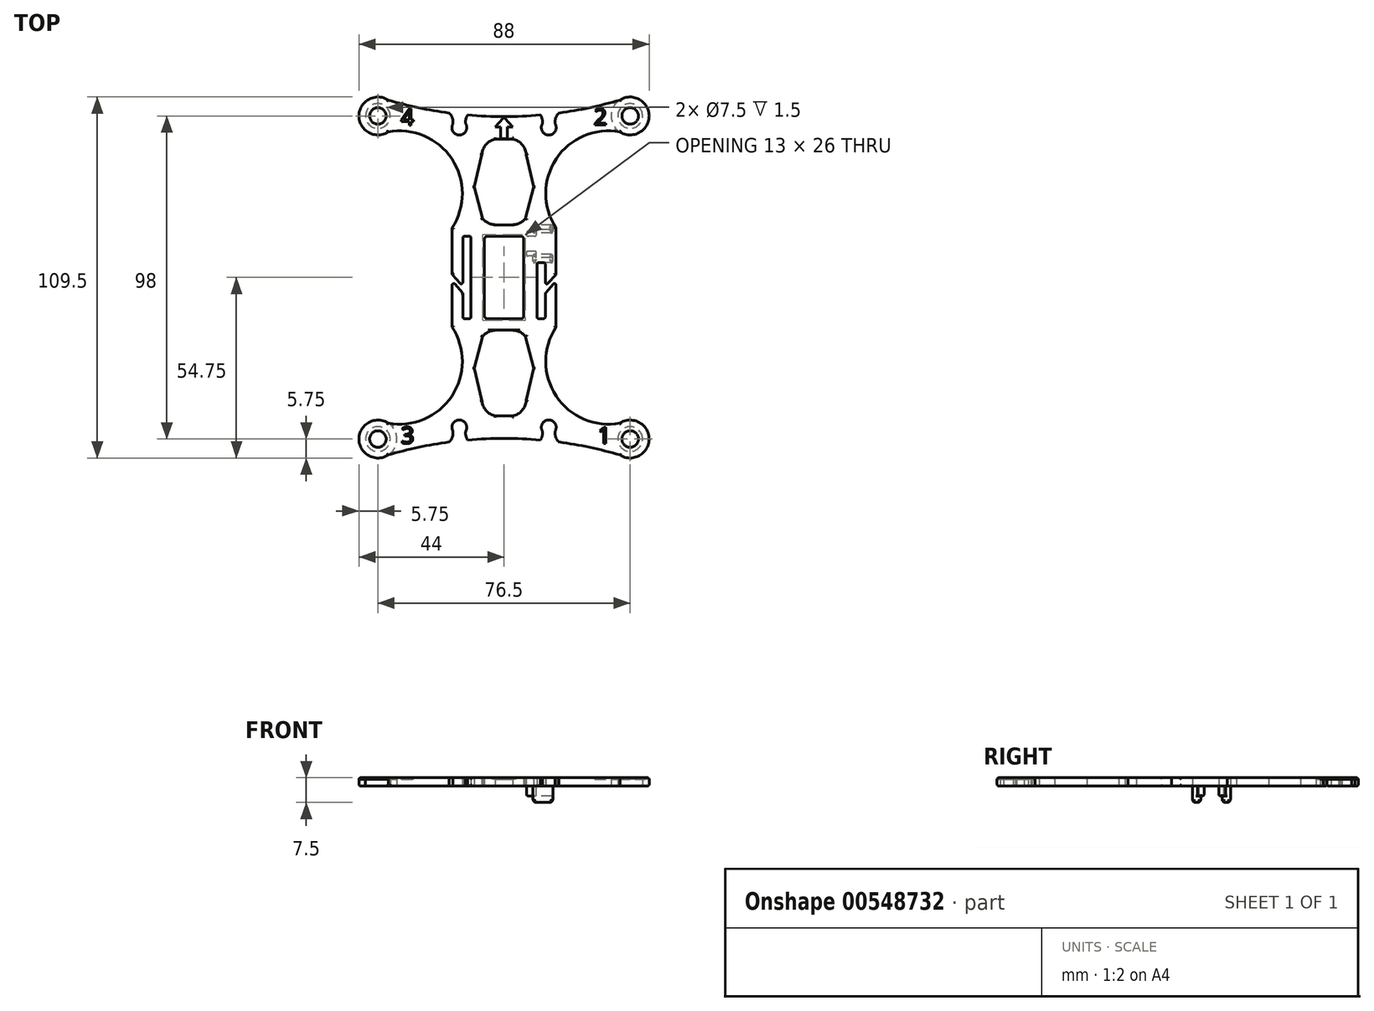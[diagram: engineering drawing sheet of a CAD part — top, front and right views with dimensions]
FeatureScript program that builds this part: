
annotation { "Feature Type Name" : "Feature", "Feature Type Description" : "" }
export const myFeature = defineFeature(function(context is Context, id is Id, definition is map)
    precondition{}
    {
        {
            var Q0;
            Q0=qCreatedBy(makeId("Top.planeOp"),FACE);
            var sketch = newSketch(context, id + "F0", { "sketchPlane" : qUnion([Q0])});
            skPoint(sketch, "E0.middle", {"position": v(0, 0) * mm});
            skCircle(sketch, "E1", {"center": v(-38.25, 49) * mm, "radius": 5.75 * mm});
            skCircle(sketch, "E2.MirrorC", {"center": v(38.25, 49) * mm, "radius": 5.75 * mm});
            skCircle(sketch, "E3.MirrorC", {"center": v(-38.25, -49) * mm, "radius": 5.75 * mm});
            skCircle(sketch, "E4.MirrorC", {"center": v(38.25, -49) * mm, "radius": 5.75 * mm});
            skArc(sketch, "E5", {"start": v(-35.12, 53.82) * mm, "mid": v(-25.97, 51.52) * mm, "end": v(-16.67, 49.9) * mm});
            skCircle(sketch, "E6", {"center": v(-38.25, 49) * mm, "radius": 3.75 * mm});
            skCircle(sketch, "E7.MirrorC", {"center": v(38.25, 49) * mm, "radius": 3.75 * mm});
            skCircle(sketch, "E8.MirrorC", {"center": v(38.25, -49) * mm, "radius": 3.75 * mm});
            skCircle(sketch, "E9.MirrorC", {"center": v(-38.25, -49) * mm, "radius": 3.75 * mm});
            skPoint(sketch, "E10.MirrorP", {"position": v(-9, -27.55) * mm});
            skArc(sketch, "E11.MirrorCS", {"start": v(-2.66, -42) * mm, "mid": v(-5.49, -40.33) * mm, "end": v(-6.7, -37.29) * mm});
            skArc(sketch, "E12.MirrorCS", {"start": v(-2.66, -16) * mm, "mid": v(-4.79, -16.51) * mm, "end": v(-6.5, -17.87) * mm});
            skLineSegment(sketch, "E13", {"start": v(-6.5, -17.87) * mm, "end": v(-9, -27.55) * mm});
            skLineSegment(sketch, "E14", {"start": v(-6.7, -37.29) * mm, "end": v(-9, -27.55) * mm});
            skArc(sketch, "E15.MirrorCS", {"start": v(2.66, -16) * mm, "mid": v(4.79, -16.51) * mm, "end": v(6.5, -17.87) * mm});
            skLineSegment(sketch, "E16.MirrorCS", {"start": v(6.5, -17.87) * mm, "end": v(9, -27.55) * mm});
            skLineSegment(sketch, "E17.MirrorCS", {"start": v(6.7, -37.29) * mm, "end": v(9, -27.55) * mm});
            skArc(sketch, "E18.MirrorCS", {"start": v(2.66, -42) * mm, "mid": v(5.49, -40.33) * mm, "end": v(6.7, -37.29) * mm});
            skLineSegment(sketch, "E19", {"start": v(-2.66, -16) * mm, "end": v(2.66, -16) * mm});
            skLineSegment(sketch, "E20", {"start": v(2.66, -42) * mm, "end": v(-2.66, -42) * mm});
            skLineSegment(sketch, "E21.MirrorCS", {"start": v(-2.66, 16) * mm, "end": v(2.66, 16) * mm});
            skArc(sketch, "E22.MirrorCS", {"start": v(-2.66, 16) * mm, "mid": v(-4.79, 16.51) * mm, "end": v(-6.5, 17.87) * mm});
            skLineSegment(sketch, "E23.MirrorCS", {"start": v(-6.5, 17.87) * mm, "end": v(-9, 27.55) * mm});
            skArc(sketch, "E24.MirrorCS", {"start": v(2.66, 16) * mm, "mid": v(4.79, 16.51) * mm, "end": v(6.5, 17.87) * mm});
            skLineSegment(sketch, "E25.MirrorCS", {"start": v(6.5, 17.87) * mm, "end": v(9, 27.55) * mm});
            skLineSegment(sketch, "E26.MirrorCS", {"start": v(-6.7, 37.29) * mm, "end": v(-9, 27.55) * mm});
            skLineSegment(sketch, "E27.MirrorCS", {"start": v(6.7, 37.29) * mm, "end": v(9, 27.55) * mm});
            skArc(sketch, "E28.MirrorCS", {"start": v(2.66, 42) * mm, "mid": v(5.49, 40.33) * mm, "end": v(6.7, 37.29) * mm});
            skLineSegment(sketch, "E29.MirrorCS", {"start": v(2.66, 42) * mm, "end": v(-2.66, 42) * mm});
            skArc(sketch, "E30.MirrorCS", {"start": v(-2.66, 42) * mm, "mid": v(-5.49, 40.33) * mm, "end": v(-6.7, 37.29) * mm});
            skArc(sketch, "E31", {"start": v(-15.79, 15) * mm, "mid": v(-15.82, 36) * mm, "end": v(-35.17, 44.14) * mm});
            skArc(sketch, "E32.MirrorCS", {"start": v(-35.12, -53.82) * mm, "mid": v(-25.97, -51.52) * mm, "end": v(-16.67, -49.9) * mm});
            skArc(sketch, "E33.MirrorCS", {"start": v(15.79, 15) * mm, "mid": v(15.82, 36) * mm, "end": v(35.17, 44.14) * mm});
            skArc(sketch, "E34.MirrorCS", {"start": v(15.79, -15) * mm, "mid": v(15.82, -36) * mm, "end": v(35.17, -44.14) * mm});
            skArc(sketch, "E35.MirrorCS", {"start": v(-15.79, -15) * mm, "mid": v(-15.82, -36) * mm, "end": v(-35.17, -44.14) * mm});
            skLineSegment(sketch, "E36", {"start": v(-15.79, 15) * mm, "end": v(15.79, 15) * mm, "construction": true});
            skLineSegment(sketch, "E37.MirrorCS", {"start": v(12, -12.5) * mm, "end": v(10.5, -12.5) * mm});
            skArc(sketch, "E38.MirrorCS", {"start": v(12.5, -12) * mm, "mid": v(12.35, -12.35) * mm, "end": v(12, -12.5) * mm});
            skArc(sketch, "E39.MirrorCS", {"start": v(10.5, -12.5) * mm, "mid": v(10.15, -12.35) * mm, "end": v(10, -12) * mm});
            skArc(sketch, "E40.trimOffspring", {"start": v(-11.03, 49.28) * mm, "mid": v(0, 48.79) * mm, "end": v(11.03, 49.28) * mm});
            skArc(sketch, "E41.MirrorCS", {"start": v(-11.6, 46.53) * mm, "mid": v(-11.6, 47.96) * mm, "end": v(-11.03, 49.28) * mm});
            skLineSegment(sketch, "E42.bottom", {"start": v(-5, 12.5) * mm, "end": v(5, 12.5) * mm});
            skLineSegment(sketch, "E42.top", {"start": v(-5, -12.5) * mm, "end": v(5, -12.5) * mm});
            skLineSegment(sketch, "E42.left", {"start": v(-6, 11.5) * mm, "end": v(-6, -11.5) * mm});
            skLineSegment(sketch, "E42.right", {"start": v(6, 11.5) * mm, "end": v(6, -11.5) * mm});
            skPoint(sketch, "E43.visualSharp", {"position": v(-6, 12.5) * mm});
            skArc(sketch, "E43.filletArc", {"start": v(-5, 12.5) * mm, "mid": v(-5.7, 12.2) * mm, "end": v(-6, 11.5) * mm});
            skArc(sketch, "E44.filletArc", {"start": v(6, 11.5) * mm, "mid": v(5.7, 12.2) * mm, "end": v(5, 12.5) * mm});
            skPoint(sketch, "E45.visualSharp", {"position": v(6, -12.5) * mm});
            skArc(sketch, "E45.filletArc", {"start": v(5, -12.5) * mm, "mid": v(5.7, -12.2) * mm, "end": v(6, -11.5) * mm});
            skPoint(sketch, "E46.visualSharp", {"position": v(-6, -12.5) * mm});
            skArc(sketch, "E46.filletArc", {"start": v(-6, -11.5) * mm, "mid": v(-5.7, -12.2) * mm, "end": v(-5, -12.5) * mm});
            skLineSegment(sketch, "E47", {"start": v(-15.79, -15) * mm, "end": v(-15.79, -2.33) * mm});
            skLineSegment(sketch, "E48", {"start": v(-15.79, 15) * mm, "end": v(-15.79, 1) * mm});
            skLineSegment(sketch, "E49.MirrorCS", {"start": v(-10, -12) * mm, "end": v(-10, 12) * mm});
            skLineSegment(sketch, "E50.MirrorCS", {"start": v(-12.5, -12) * mm, "end": v(-12.5, -4.77) * mm});
            skLineSegment(sketch, "E51.MirrorCS", {"start": v(-12, 12.5) * mm, "end": v(-10.5, 12.5) * mm});
            skArc(sketch, "E52.MirrorCS", {"start": v(-10, 12) * mm, "mid": v(-10.15, 12.35) * mm, "end": v(-10.5, 12.5) * mm});
            skArc(sketch, "E53.MirrorCS", {"start": v(-12, 12.5) * mm, "mid": v(-12.35, 12.35) * mm, "end": v(-12.5, 12) * mm});
            skArc(sketch, "E54.MirrorCS", {"start": v(-10.5, -12.5) * mm, "mid": v(-10.15, -12.35) * mm, "end": v(-10, -12) * mm});
            skLineSegment(sketch, "E55.MirrorCS", {"start": v(-12, -12.5) * mm, "end": v(-10.5, -12.5) * mm});
            skArc(sketch, "E56.MirrorCS", {"start": v(-12.5, -12) * mm, "mid": v(-12.35, -12.35) * mm, "end": v(-12, -12.5) * mm});
            skLineSegment(sketch, "E57", {"start": v(-14.91, -2) * mm, "end": v(-12.5, -4.77) * mm});
            skLineSegment(sketch, "E58", {"start": v(-15.79, 1) * mm, "end": v(-13.38, -1.76) * mm});
            skLineSegment(sketch, "E59.trimOffspring", {"start": v(-12.5, -1.43) * mm, "end": v(-12.5, 12) * mm});
            skPoint(sketch, "E60.visualSharp", {"position": v(-15.79, -1) * mm});
            skArc(sketch, "E60.filletArc", {"start": v(-14.91, -2) * mm, "mid": v(-15.47, -1.86) * mm, "end": v(-15.79, -2.33) * mm});
            skArc(sketch, "E61.filletArc", {"start": v(-13.38, -1.76) * mm, "mid": v(-12.82, -1.9) * mm, "end": v(-12.5, -1.43) * mm});
            skLineSegment(sketch, "E62.MirrorCS", {"start": v(12.5, -12) * mm, "end": v(12.5, -4.77) * mm});
            skLineSegment(sketch, "E63.MirrorCS", {"start": v(10, -12) * mm, "end": v(10, 4) * mm});
            skLineSegment(sketch, "E64.MirrorCS", {"start": v(14.91, -2) * mm, "end": v(12.5, -4.77) * mm});
            skLineSegment(sketch, "E65.MirrorCS", {"start": v(15.79, -15) * mm, "end": v(15.79, -2.33) * mm});
            skArc(sketch, "E66.MirrorCS", {"start": v(14.91, -2) * mm, "mid": v(15.47, -1.86) * mm, "end": v(15.79, -2.33) * mm});
            skArc(sketch, "E67.MirrorCS", {"start": v(13.38, -1.76) * mm, "mid": v(12.82, -1.9) * mm, "end": v(12.5, -1.43) * mm});
            skLineSegment(sketch, "E68.MirrorCS", {"start": v(12.5, -1.43) * mm, "end": v(12.5, 4) * mm});
            skLineSegment(sketch, "E69.MirrorCS", {"start": v(15.79, 1) * mm, "end": v(13.38, -1.76) * mm});
            skLineSegment(sketch, "E70.MirrorCS", {"start": v(15.79, 15) * mm, "end": v(15.79, 1) * mm});
            skPoint(sketch, "E71", {"position": v(10, 4.5) * mm});
            skPoint(sketch, "E72", {"position": v(12.5, 4.5) * mm});
            skLineSegment(sketch, "E73", {"start": v(10.5, 4.5) * mm, "end": v(12, 4.5) * mm});
            skArc(sketch, "E74.filletArc", {"start": v(10.5, 4.5) * mm, "mid": v(10.15, 4.35) * mm, "end": v(10, 4) * mm});
            skArc(sketch, "E75.filletArc", {"start": v(12.5, 4) * mm, "mid": v(12.35, 4.35) * mm, "end": v(12, 4.5) * mm});
            skPoint(sketch, "E76.visualSharp", {"position": v(8.79, 4.5) * mm});
            skPoint(sketch, "E77.visualSharp", {"position": v(14.79, 4.5) * mm});
            skArc(sketch, "E78.trimOffspring", {"start": v(16.67, 49.9) * mm, "mid": v(25.97, 51.52) * mm, "end": v(35.12, 53.82) * mm});
            skArc(sketch, "E79.trimOffspring", {"start": v(16.67, -49.9) * mm, "mid": v(25.97, -51.52) * mm, "end": v(35.12, -53.82) * mm});
            skArc(sketch, "E80.trimOffspring", {"start": v(-11.03, -49.28) * mm, "mid": v(0, -48.79) * mm, "end": v(11.03, -49.28) * mm});
            skLineSegment(sketch, "E81", {"start": v(17.22, 49.98) * mm, "end": v(17.22, 49.98) * mm});
            skLineSegment(sketch, "E82.MirrorCS", {"start": v(17.22, -49.98) * mm, "end": v(17.22, -49.98) * mm});
            skArc(sketch, "E83.MirrorCS", {"start": v(-15.54, 46.53) * mm, "mid": v(-15.65, 48.37) * mm, "end": v(-16.67, 49.9) * mm});
            skArc(sketch, "E84.trimOffspring", {"start": v(-15.54, 46.53) * mm, "mid": v(-13.57, 43.2) * mm, "end": v(-11.6, 46.53) * mm});
            skArc(sketch, "E85.MirrorCS", {"start": v(11.6, 46.53) * mm, "mid": v(11.6, 47.96) * mm, "end": v(11.03, 49.28) * mm});
            skArc(sketch, "E86.MirrorCS", {"start": v(15.54, 46.53) * mm, "mid": v(13.57, 43.2) * mm, "end": v(11.6, 46.53) * mm});
            skArc(sketch, "E87.MirrorCS", {"start": v(15.54, 46.53) * mm, "mid": v(15.65, 48.37) * mm, "end": v(16.67, 49.9) * mm});
            skArc(sketch, "E88.MirrorCS", {"start": v(15.54, -46.53) * mm, "mid": v(13.57, -43.2) * mm, "end": v(11.6, -46.53) * mm});
            skArc(sketch, "E89.MirrorCS", {"start": v(15.54, -46.53) * mm, "mid": v(15.65, -48.37) * mm, "end": v(16.67, -49.9) * mm});
            skArc(sketch, "E90.MirrorCS", {"start": v(11.6, -46.53) * mm, "mid": v(11.6, -47.96) * mm, "end": v(11.03, -49.28) * mm});
            skArc(sketch, "E91.MirrorCS", {"start": v(-15.54, -46.53) * mm, "mid": v(-15.65, -48.37) * mm, "end": v(-16.67, -49.9) * mm});
            skArc(sketch, "E92.MirrorCS", {"start": v(-11.6, -46.53) * mm, "mid": v(-11.6, -47.96) * mm, "end": v(-11.03, -49.28) * mm});
            skArc(sketch, "E93.MirrorCS", {"start": v(-15.54, -46.53) * mm, "mid": v(-13.57, -43.2) * mm, "end": v(-11.6, -46.53) * mm});
            skSolve(sketch);
        }
        {
            var Q0;
            {var subQ4=sQuery(id+"F0.wireOp",EDGE,"E5");Q0=makeQuery(id+"F0.imprint","IMPRINT",FACE,{"disambiguationData":[TD([[makeQuery(id+"F0.imprint","IMPRINT",EDGE,{"derivedFrom":subQ4}),-1.0]])]});}
            var Q1;
            {var subQ0=sQuery(id+"F0.wireOp",EDGE,"7a08c846-7200-404a-ab22-a396ae0e95b40.MirrorCS");Q1=makeQuery(id+"F0.imprint","IMPRINT",FACE,{"disambiguationData":[TD([[makeQuery(id+"F0.imprint","IMPRINT",EDGE,{"derivedFrom":subQ0}),-1.0]])]});}
            var Q2;
            {var subQ0=sQuery(id+"F0.wireOp",EDGE,"SV39OC4L-nHPT-JrW3-9Lr1-tMvvluVvlcrm");Q2=makeQuery(id+"F0.imprint","IMPRINT",FACE,{"disambiguationData":[TD([[makeQuery(id+"F0.imprint","IMPRINT",EDGE,{"derivedFrom":subQ0}),1.0]])]});}
            var Q3;
            {var subQ2=sQuery(id+"F0.wireOp",EDGE,"KmvPTI4Y-Ru9T-GGZq-2kg1-KeB8K268cKMw.top");Q3=makeQuery(id+"F0.imprint","IMPRINT",FACE,{"disambiguationData":[TD([[makeQuery(id+"F0.imprint","IMPRINT",EDGE,{"derivedFrom":subQ2}),-1.0]])]});}
            var Q4;
            Q4=makeQuery(id+"F0.imprint","IMPRINT",FACE,{"disambiguationData":[TD([[makeQuery(id+"F0.imprint","IMPRINT",EDGE,{"derivedFrom":sQuery(id+"F0.wireOp",EDGE,"TM0b15PC-G09Y-eCJG-wMI8-OMJ6jJeQZKML.top")}),1.0]])]});
            var Q5;
            Q5=makeQuery(id+"F0.imprint","IMPRINT",FACE,{"disambiguationData":[TD([[makeQuery(id+"F0.imprint","IMPRINT",EDGE,{"derivedFrom":sQuery(id+"F0.wireOp",EDGE,"3d6d2522-cb81-429b-89e0-43078ca379200.MirrorCS")}),-1.0]])]});
            var Q6;
            {var subQ1=sQuery(id+"F0.wireOp",EDGE,"f26be708-061c-449e-934f-b77e1b1d895a0.MirrorCS");Q6=makeQuery(id+"F0.imprint","IMPRINT",FACE,{"disambiguationData":[TD([[makeQuery(id+"F0.imprint","IMPRINT",EDGE,{"derivedFrom":subQ1}),-1.0]])]});}
            extrude(context, id + "F1", {"entities" : qUnion([Q0, Q1, Q2, Q3, Q4, Q5, Q6]), "depth" : 2.5 * mm});
        }
        {
            var Q0;
            Q0=makeQuery(id+"F0.imprint","IMPRINT",FACE,{"disambiguationData":[TD([[makeQuery(id+"F0.imprint","IMPRINT",EDGE,{"derivedFrom":sQuery(id+"F0.wireOp",EDGE,"E6")}),-1.0]])]});
            var Q1;
            Q1=makeQuery(id+"F0.imprint","IMPRINT",FACE,{"disambiguationData":[TD([[makeQuery(id+"F0.imprint","IMPRINT",EDGE,{"derivedFrom":sQuery(id+"F0.wireOp",EDGE,"E7.MirrorC")}),1.0]])]});
            var Q2;
            Q2=makeQuery(id+"F0.imprint","IMPRINT",FACE,{"disambiguationData":[TD([[makeQuery(id+"F0.imprint","IMPRINT",EDGE,{"derivedFrom":sQuery(id+"F0.wireOp",EDGE,"E8.MirrorC")}),-1.0]])]});
            var Q3;
            Q3=makeQuery(id+"F0.imprint","IMPRINT",FACE,{"disambiguationData":[TD([[makeQuery(id+"F0.imprint","IMPRINT",EDGE,{"derivedFrom":sQuery(id+"F0.wireOp",EDGE,"E9.MirrorC")}),1.0]])]});
            extrude(context, id + "F2", {"entities" : qUnion([Q0, Q1, Q2, Q3]), "operationType" : NewBodyOperationType.ADD, "depth" : 2 * mm});
        }
        {
            var Q0;
            Q0=makeQuery(id+"F1.opExtrude","CAP_FACE",FACE,{"disambiguationData":[OSD([sQuery(id+"F0.wireOp",EDGE,"E1"),sQuery(id+"F0.wireOp",EDGE,"E2.MirrorC"),sQuery(id+"F0.wireOp",EDGE,"E3.MirrorC"),sQuery(id+"F0.wireOp",EDGE,"E4.MirrorC"),sQuery(id+"F0.wireOp",EDGE,"E5"),sQuery(id+"F0.wireOp",EDGE,"E6"),sQuery(id+"F0.wireOp",EDGE,"E7.MirrorC"),sQuery(id+"F0.wireOp",EDGE,"E8.MirrorC"),sQuery(id+"F0.wireOp",EDGE,"E9.MirrorC"),sQuery(id+"F0.wireOp",EDGE,"vB4YpJxw-nM1r-KAMU-Z2z7-AA1Xbjjr12VQ"),sQuery(id+"F0.wireOp",EDGE,"e54bd452-817c-44b1-b4a1-4a82a5b737490.MirrorC"),sQuery(id+"F0.wireOp",EDGE,"5ae8c34d-aa19-45d0-b816-4b0481c35e6e0.MirrorC"),sQuery(id+"F0.wireOp",EDGE,"3a3e3443-e76c-4b3f-931a-bba0a9ca54bb0.MirrorC"),sQuery(id+"F0.wireOp",EDGE,"E11.MirrorCS"),sQuery(id+"F0.wireOp",EDGE,"E12.MirrorCS"),sQuery(id+"F0.wireOp",EDGE,"E13"),sQuery(id+"F0.wireOp",EDGE,"E14"),sQuery(id+"F0.wireOp",EDGE,"E15.MirrorCS"),sQuery(id+"F0.wireOp",EDGE,"E16.MirrorCS"),sQuery(id+"F0.wireOp",EDGE,"E17.MirrorCS"),sQuery(id+"F0.wireOp",EDGE,"E18.MirrorCS"),sQuery(id+"F0.wireOp",EDGE,"E19"),sQuery(id+"F0.wireOp",EDGE,"E20"),sQuery(id+"F0.wireOp",EDGE,"E21.MirrorCS"),sQuery(id+"F0.wireOp",EDGE,"E22.MirrorCS"),sQuery(id+"F0.wireOp",EDGE,"E23.MirrorCS"),sQuery(id+"F0.wireOp",EDGE,"E24.MirrorCS"),sQuery(id+"F0.wireOp",EDGE,"E25.MirrorCS"),sQuery(id+"F0.wireOp",EDGE,"E26.MirrorCS"),sQuery(id+"F0.wireOp",EDGE,"E27.MirrorCS"),sQuery(id+"F0.wireOp",EDGE,"E28.MirrorCS"),sQuery(id+"F0.wireOp",EDGE,"E29.MirrorCS"),sQuery(id+"F0.wireOp",EDGE,"E30.MirrorCS"),sQuery(id+"F0.wireOp",EDGE,"E31"),sQuery(id+"F0.wireOp",EDGE,"E32.MirrorCS"),sQuery(id+"F0.wireOp",EDGE,"E33.MirrorCS"),sQuery(id+"F0.wireOp",EDGE,"E34.MirrorCS"),sQuery(id+"F0.wireOp",EDGE,"E35.MirrorCS"),sQuery(id+"F0.wireOp",EDGE,"fVDweLas-wsoK-wS6S-1z9Y-dXXYinH5IBTg"),sQuery(id+"F0.wireOp",EDGE,"DgQ3zJUJ-pF02-0TgB-KWvi-qXfrHXNG7Bep.bottom"),sQuery(id+"F0.wireOp",EDGE,"DgQ3zJUJ-pF02-0TgB-KWvi-qXfrHXNG7Bep.top"),sQuery(id+"F0.wireOp",EDGE,"DgQ3zJUJ-pF02-0TgB-KWvi-qXfrHXNG7Bep.left"),sQuery(id+"F0.wireOp",EDGE,"DgQ3zJUJ-pF02-0TgB-KWvi-qXfrHXNG7Bep.right"),sQuery(id+"F0.wireOp",EDGE,"c76fb391-d7de-4dc3-a68f-2a06cb2f6573.filletArc"),sQuery(id+"F0.wireOp",EDGE,"5654feee-e0ec-4d14-bcde-d39bc1d4a277.filletArc"),sQuery(id+"F0.wireOp",EDGE,"a181469e-c1a0-4d89-87a1-cba4924c182a.filletArc"),sQuery(id+"F0.wireOp",EDGE,"6285ec27-b856-43d4-bfe6-c4aa6bb2cc4e.filletArc"),sQuery(id+"F0.wireOp",EDGE,"E37.MirrorCS"),sQuery(id+"F0.wireOp",EDGE,"E38.MirrorCS"),sQuery(id+"F0.wireOp",EDGE,"E39.MirrorCS"),sQuery(id+"F0.wireOp",EDGE,"6c157492-324c-4fe9-82e5-da5673b074dd0.MirrorCS"),sQuery(id+"F0.wireOp",EDGE,"5ab077b0-c7e9-45b7-be53-f71d1ae10c3f0.MirrorCS"),sQuery(id+"F0.wireOp",EDGE,"fc55cce6-b858-4ce9-87a1-b3bd53c235ab0.MirrorCS"),sQuery(id+"F0.wireOp",EDGE,"9f491082-fd4d-4411-bae9-10bea509d7400.MirrorCS"),sQuery(id+"F0.wireOp",EDGE,"1b0662fc-7704-42c9-b5fa-9ce22a18d3f90.MirrorCS"),sQuery(id+"F0.wireOp",EDGE,"QFYX3ccx-0vfA-8Ihh-7p7o-tATHIodxN48p"),sQuery(id+"F0.wireOp",EDGE,"E40.trimOffspring"),sQuery(id+"F0.wireOp",EDGE,"qH3YTvKd-Peeo-Apzx-g0Uu-npIK0QSimt1m"),sQuery(id+"F0.wireOp",EDGE,"HBzP5cjg-J4kx-zMse-p9Wa-D2NjmpWyf6zF"),sQuery(id+"F0.wireOp",EDGE,"b30a117b-d75a-4502-b387-7b125c7515d1.trimOffspring"),sQuery(id+"F0.wireOp",EDGE,"Q6oGcjuH-qqtT-cDzR-LXAg-flI4N5uVv7ns"),sQuery(id+"F0.wireOp",EDGE,"E41.MirrorCS"),sQuery(id+"F0.wireOp",EDGE,"NQUfp69C-25it-PKYB-2tBc-24tSypLDHoPc"),sQuery(id+"F0.wireOp",EDGE,"c989e6c5-f976-4a01-a2df-d995f657efa90.MirrorCS"),sQuery(id+"F0.wireOp",EDGE,"15c0fab1-d19e-4163-b076-96272f6b97990.MirrorCS"),sQuery(id+"F0.wireOp",EDGE,"37e26e7e-321b-4c47-af7c-8b72d8fa4a340.MirrorCS"),sQuery(id+"F0.wireOp",EDGE,"0fc43aed-00d9-4609-b4de-8f51d0ed3c1b0.MirrorCS"),sQuery(id+"F0.wireOp",EDGE,"ec73fb21-01e8-4369-aab7-f5da74862bec0.MirrorCS"),sQuery(id+"F0.wireOp",EDGE,"92f736b5-5a78-439e-ae92-a389169262630.MirrorCS"),sQuery(id+"F0.wireOp",EDGE,"d2bba0ee-929f-40cb-a0b9-0c6ccd42c60c0.MirrorCS"),sQuery(id+"F0.wireOp",EDGE,"95becd90-c284-490f-9980-00c66b97ee920.MirrorCS"),sQuery(id+"F0.wireOp",EDGE,"17a50fb4-b6d3-4921-a8fa-819a7e347bdf0.MirrorCS"),sQuery(id+"F0.wireOp",EDGE,"0a836e34-2154-49af-98e0-05fdf2c9219c0.MirrorCS"),sQuery(id+"F0.wireOp",EDGE,"69461dee-d267-421c-9efa-fca9b703b25c0.MirrorCS"),sQuery(id+"F0.wireOp",EDGE,"E42.bottom"),sQuery(id+"F0.wireOp",EDGE,"E42.top"),sQuery(id+"F0.wireOp",EDGE,"E42.left"),sQuery(id+"F0.wireOp",EDGE,"E42.right"),sQuery(id+"F0.wireOp",EDGE,"E43.filletArc"),sQuery(id+"F0.wireOp",EDGE,"E44.filletArc"),sQuery(id+"F0.wireOp",EDGE,"E45.filletArc"),sQuery(id+"F0.wireOp",EDGE,"E46.filletArc")])],"isStart":false});
            var sketch = newSketch(context, id + "F3", { "sketchPlane" : qUnion([Q0])});
            skLineSegment(sketch, "E94", {"start": v(-1, 42.11) * mm, "end": v(-1, 45.61) * mm});
            skLineSegment(sketch, "E95", {"start": v(-1, 45.61) * mm, "end": v(-2.66, 45.61) * mm});
            skLineSegment(sketch, "E96", {"start": v(-2.66, 45.61) * mm, "end": v(0, 48.6) * mm});
            skLineSegment(sketch, "E97.MirrorCS", {"start": v(2.66, 45.61) * mm, "end": v(0, 48.6) * mm});
            skLineSegment(sketch, "E98.MirrorCS", {"start": v(1, 45.61) * mm, "end": v(2.66, 45.61) * mm});
            skLineSegment(sketch, "E99.MirrorCS", {"start": v(1, 42.11) * mm, "end": v(1, 45.61) * mm});
            skLineSegment(sketch, "E100", {"start": v(-1, 42.11) * mm, "end": v(1, 42.11) * mm});
            skText(sketch, "E101", { "text": "1", "fontName": "OpenSans-Regular.ttf"});
            skText(sketch, "E102", { "text": "3", "fontName": "OpenSans-Regular.ttf"});
            skText(sketch, "E103", { "text": "2", "fontName": "OpenSans-Regular.ttf"});
            skText(sketch, "E104", { "text": "4", "fontName": "OpenSans-Regular.ttf"});
            const initialGuessF3  = {"E101": [0.02838, -0.05039, 1, 0, 0.005], "E102": [-0.03125, -0.05033, 1, 0, 0.005], "E103": [0.0272, 0.04623, 1, 0, 0.005], "E104": [-0.03125, 0.0462, 1, 0, 0.005]};
            skSetInitialGuess(sketch, initialGuessF3);
            skSolve(sketch);
        }
        {
            var Q0;
            Q0=qSketchRegion(id+"F3",true);
            extrude(context, id + "F4", {"entities" : qUnion([Q0]), "operationType" : NewBodyOperationType.REMOVE, "oppositeDirection" : true, "depth" : .5 * mm});
        }
        {
            var Q0;
            Q0=makeQuery(id+"F1.opExtrude","CAP_FACE",FACE,{"disambiguationData":[OSD([sQuery(id+"F0.wireOp",EDGE,"E1"),sQuery(id+"F0.wireOp",EDGE,"E2.MirrorC"),sQuery(id+"F0.wireOp",EDGE,"E3.MirrorC"),sQuery(id+"F0.wireOp",EDGE,"E4.MirrorC"),sQuery(id+"F0.wireOp",EDGE,"E5"),sQuery(id+"F0.wireOp",EDGE,"E6"),sQuery(id+"F0.wireOp",EDGE,"E7.MirrorC"),sQuery(id+"F0.wireOp",EDGE,"E8.MirrorC"),sQuery(id+"F0.wireOp",EDGE,"E9.MirrorC"),sQuery(id+"F0.wireOp",EDGE,"vB4YpJxw-nM1r-KAMU-Z2z7-AA1Xbjjr12VQ"),sQuery(id+"F0.wireOp",EDGE,"e54bd452-817c-44b1-b4a1-4a82a5b737490.MirrorC"),sQuery(id+"F0.wireOp",EDGE,"5ae8c34d-aa19-45d0-b816-4b0481c35e6e0.MirrorC"),sQuery(id+"F0.wireOp",EDGE,"3a3e3443-e76c-4b3f-931a-bba0a9ca54bb0.MirrorC"),sQuery(id+"F0.wireOp",EDGE,"E11.MirrorCS"),sQuery(id+"F0.wireOp",EDGE,"E12.MirrorCS"),sQuery(id+"F0.wireOp",EDGE,"E13"),sQuery(id+"F0.wireOp",EDGE,"E14"),sQuery(id+"F0.wireOp",EDGE,"E15.MirrorCS"),sQuery(id+"F0.wireOp",EDGE,"E16.MirrorCS"),sQuery(id+"F0.wireOp",EDGE,"E17.MirrorCS"),sQuery(id+"F0.wireOp",EDGE,"E18.MirrorCS"),sQuery(id+"F0.wireOp",EDGE,"E19"),sQuery(id+"F0.wireOp",EDGE,"E20"),sQuery(id+"F0.wireOp",EDGE,"E21.MirrorCS"),sQuery(id+"F0.wireOp",EDGE,"E22.MirrorCS"),sQuery(id+"F0.wireOp",EDGE,"E23.MirrorCS"),sQuery(id+"F0.wireOp",EDGE,"E24.MirrorCS"),sQuery(id+"F0.wireOp",EDGE,"E25.MirrorCS"),sQuery(id+"F0.wireOp",EDGE,"E26.MirrorCS"),sQuery(id+"F0.wireOp",EDGE,"E27.MirrorCS"),sQuery(id+"F0.wireOp",EDGE,"E28.MirrorCS"),sQuery(id+"F0.wireOp",EDGE,"E29.MirrorCS"),sQuery(id+"F0.wireOp",EDGE,"E30.MirrorCS"),sQuery(id+"F0.wireOp",EDGE,"E31"),sQuery(id+"F0.wireOp",EDGE,"E32.MirrorCS"),sQuery(id+"F0.wireOp",EDGE,"E33.MirrorCS"),sQuery(id+"F0.wireOp",EDGE,"E34.MirrorCS"),sQuery(id+"F0.wireOp",EDGE,"E35.MirrorCS"),sQuery(id+"F0.wireOp",EDGE,"E37.MirrorCS"),sQuery(id+"F0.wireOp",EDGE,"E38.MirrorCS"),sQuery(id+"F0.wireOp",EDGE,"E39.MirrorCS"),sQuery(id+"F0.wireOp",EDGE,"E40.trimOffspring"),sQuery(id+"F0.wireOp",EDGE,"qH3YTvKd-Peeo-Apzx-g0Uu-npIK0QSimt1m"),sQuery(id+"F0.wireOp",EDGE,"HBzP5cjg-J4kx-zMse-p9Wa-D2NjmpWyf6zF"),sQuery(id+"F0.wireOp",EDGE,"b30a117b-d75a-4502-b387-7b125c7515d1.trimOffspring"),sQuery(id+"F0.wireOp",EDGE,"Q6oGcjuH-qqtT-cDzR-LXAg-flI4N5uVv7ns"),sQuery(id+"F0.wireOp",EDGE,"E41.MirrorCS"),sQuery(id+"F0.wireOp",EDGE,"NQUfp69C-25it-PKYB-2tBc-24tSypLDHoPc"),sQuery(id+"F0.wireOp",EDGE,"c989e6c5-f976-4a01-a2df-d995f657efa90.MirrorCS"),sQuery(id+"F0.wireOp",EDGE,"15c0fab1-d19e-4163-b076-96272f6b97990.MirrorCS"),sQuery(id+"F0.wireOp",EDGE,"37e26e7e-321b-4c47-af7c-8b72d8fa4a340.MirrorCS"),sQuery(id+"F0.wireOp",EDGE,"0fc43aed-00d9-4609-b4de-8f51d0ed3c1b0.MirrorCS"),sQuery(id+"F0.wireOp",EDGE,"ec73fb21-01e8-4369-aab7-f5da74862bec0.MirrorCS"),sQuery(id+"F0.wireOp",EDGE,"92f736b5-5a78-439e-ae92-a389169262630.MirrorCS"),sQuery(id+"F0.wireOp",EDGE,"d2bba0ee-929f-40cb-a0b9-0c6ccd42c60c0.MirrorCS"),sQuery(id+"F0.wireOp",EDGE,"95becd90-c284-490f-9980-00c66b97ee920.MirrorCS"),sQuery(id+"F0.wireOp",EDGE,"17a50fb4-b6d3-4921-a8fa-819a7e347bdf0.MirrorCS"),sQuery(id+"F0.wireOp",EDGE,"0a836e34-2154-49af-98e0-05fdf2c9219c0.MirrorCS"),sQuery(id+"F0.wireOp",EDGE,"69461dee-d267-421c-9efa-fca9b703b25c0.MirrorCS"),sQuery(id+"F0.wireOp",EDGE,"E42.bottom"),sQuery(id+"F0.wireOp",EDGE,"E42.top"),sQuery(id+"F0.wireOp",EDGE,"E42.left"),sQuery(id+"F0.wireOp",EDGE,"E42.right"),sQuery(id+"F0.wireOp",EDGE,"E43.filletArc"),sQuery(id+"F0.wireOp",EDGE,"E44.filletArc"),sQuery(id+"F0.wireOp",EDGE,"E45.filletArc"),sQuery(id+"F0.wireOp",EDGE,"E46.filletArc"),sQuery(id+"F0.wireOp",EDGE,"E47"),sQuery(id+"F0.wireOp",EDGE,"E48"),sQuery(id+"F0.wireOp",EDGE,"E49.MirrorCS"),sQuery(id+"F0.wireOp",EDGE,"E50.MirrorCS"),sQuery(id+"F0.wireOp",EDGE,"E51.MirrorCS"),sQuery(id+"F0.wireOp",EDGE,"E52.MirrorCS"),sQuery(id+"F0.wireOp",EDGE,"E53.MirrorCS"),sQuery(id+"F0.wireOp",EDGE,"E54.MirrorCS"),sQuery(id+"F0.wireOp",EDGE,"E55.MirrorCS"),sQuery(id+"F0.wireOp",EDGE,"E56.MirrorCS"),sQuery(id+"F0.wireOp",EDGE,"E57"),sQuery(id+"F0.wireOp",EDGE,"E58"),sQuery(id+"F0.wireOp",EDGE,"E59.trimOffspring"),sQuery(id+"F0.wireOp",EDGE,"E60.filletArc"),sQuery(id+"F0.wireOp",EDGE,"E61.filletArc"),sQuery(id+"F0.wireOp",EDGE,"E62.MirrorCS"),sQuery(id+"F0.wireOp",EDGE,"E63.MirrorCS"),sQuery(id+"F0.wireOp",EDGE,"E64.MirrorCS"),sQuery(id+"F0.wireOp",EDGE,"E65.MirrorCS"),sQuery(id+"F0.wireOp",EDGE,"E66.MirrorCS"),sQuery(id+"F0.wireOp",EDGE,"E67.MirrorCS"),sQuery(id+"F0.wireOp",EDGE,"E68.MirrorCS"),sQuery(id+"F0.wireOp",EDGE,"E69.MirrorCS"),sQuery(id+"F0.wireOp",EDGE,"E70.MirrorCS"),sQuery(id+"F0.wireOp",EDGE,"E73"),sQuery(id+"F0.wireOp",EDGE,"E74.filletArc"),sQuery(id+"F0.wireOp",EDGE,"E75.filletArc")])],"isStart":true});
            var sketch = newSketch(context, id + "F5", { "sketchPlane" : qUnion([Q0])});
            skLineSegment(sketch, "E105.bottom", {"start": v(14.29, -4.5) * mm, "end": v(9.29, -4.5) * mm});
            skLineSegment(sketch, "E105.top", {"start": v(14.29, -6) * mm, "end": v(9.79, -6) * mm});
            skLineSegment(sketch, "E105.left", {"start": v(14.79, -5) * mm, "end": v(14.79, -5.5) * mm});
            skLineSegment(sketch, "E105.right", {"start": v(8.79, -5) * mm, "end": v(8.79, -6) * mm});
            skLineSegment(sketch, "E106.left", {"start": v(9.79, -6) * mm, "end": v(9.79, -6.5) * mm});
            skLineSegment(sketch, "E106.right", {"start": v(8.79, -6) * mm, "end": v(8.79, -6.5) * mm});
            skLineSegment(sketch, "E107.bottom", {"start": v(8.79, -6.5) * mm, "end": v(7.29, -6.5) * mm});
            skLineSegment(sketch, "E107.top", {"start": v(9.29, -8) * mm, "end": v(7.29, -8) * mm});
            skLineSegment(sketch, "E107.left", {"start": v(9.79, -6.5) * mm, "end": v(9.79, -7.5) * mm});
            skLineSegment(sketch, "E107.right", {"start": v(6.79, -7) * mm, "end": v(6.79, -7.5) * mm});
            skPoint(sketch, "E108.visualSharp", {"position": v(6.79, -6.5) * mm});
            skArc(sketch, "E108.filletArc", {"start": v(7.29, -6.5) * mm, "mid": v(6.94, -6.65) * mm, "end": v(6.79, -7) * mm});
            skPoint(sketch, "E109.visualSharp", {"position": v(6.79, -8) * mm});
            skArc(sketch, "E109.filletArc", {"start": v(6.79, -7.5) * mm, "mid": v(6.94, -7.85) * mm, "end": v(7.29, -8) * mm});
            skPoint(sketch, "E110.visualSharp", {"position": v(9.79, -8) * mm});
            skArc(sketch, "E110.filletArc", {"start": v(9.29, -8) * mm, "mid": v(9.64, -7.85) * mm, "end": v(9.79, -7.5) * mm});
            skPoint(sketch, "E111.visualSharp", {"position": v(14.79, -6) * mm});
            skArc(sketch, "E111.filletArc", {"start": v(14.29, -6) * mm, "mid": v(14.64, -5.85) * mm, "end": v(14.79, -5.5) * mm});
            skPoint(sketch, "E112", {"position": v(14.79, -4.5) * mm});
            skArc(sketch, "E113.filletArc", {"start": v(14.79, -5) * mm, "mid": v(14.64, -4.65) * mm, "end": v(14.29, -4.5) * mm});
            skPoint(sketch, "E114", {"position": v(8.79, -4.5) * mm});
            skArc(sketch, "E115.filletArc", {"start": v(9.29, -4.5) * mm, "mid": v(8.94, -4.65) * mm, "end": v(8.79, -5) * mm});
            skLineSegment(sketch, "E116", {"start": v(6.79, -8) * mm, "end": v(6.79, -12.5) * mm, "construction": true});
            skPoint(sketch, "E117", {"position": v(6.79, -10.25) * mm});
            skLineSegment(sketch, "E118", {"start": v(6.79, -10.25) * mm, "end": v(15.79, -10.25) * mm, "construction": true});
            skLineSegment(sketch, "E119.MirrorCS", {"start": v(9.29, -12.5) * mm, "end": v(7.29, -12.5) * mm});
            skArc(sketch, "E120.MirrorCS", {"start": v(6.79, -13) * mm, "mid": v(6.94, -12.65) * mm, "end": v(7.29, -12.5) * mm});
            skLineSegment(sketch, "E121.MirrorCS", {"start": v(6.79, -13.5) * mm, "end": v(6.79, -13) * mm});
            skArc(sketch, "E122.MirrorCS", {"start": v(7.29, -14) * mm, "mid": v(6.94, -13.85) * mm, "end": v(6.79, -13.5) * mm});
            skLineSegment(sketch, "E123.MirrorCS", {"start": v(8.79, -14) * mm, "end": v(7.29, -14) * mm});
            skLineSegment(sketch, "E124.MirrorCS", {"start": v(9.79, -14) * mm, "end": v(9.79, -13) * mm});
            skArc(sketch, "E125.MirrorCS", {"start": v(9.29, -12.5) * mm, "mid": v(9.64, -12.65) * mm, "end": v(9.79, -13) * mm});
            skLineSegment(sketch, "E126.MirrorCS", {"start": v(8.79, -14.5) * mm, "end": v(8.79, -14) * mm});
            skLineSegment(sketch, "E127.MirrorCS", {"start": v(9.79, -14.5) * mm, "end": v(9.79, -14) * mm});
            skLineSegment(sketch, "E128.MirrorCS", {"start": v(8.79, -15.5) * mm, "end": v(8.79, -14.5) * mm});
            skArc(sketch, "E129.MirrorCS", {"start": v(9.29, -16) * mm, "mid": v(8.94, -15.85) * mm, "end": v(8.79, -15.5) * mm});
            skLineSegment(sketch, "E130.MirrorCS", {"start": v(14.29, -14.5) * mm, "end": v(9.79, -14.5) * mm});
            skLineSegment(sketch, "E131.MirrorCS", {"start": v(14.29, -16) * mm, "end": v(9.29, -16) * mm});
            skArc(sketch, "E132.MirrorCS", {"start": v(14.29, -14.5) * mm, "mid": v(14.64, -14.65) * mm, "end": v(14.79, -15) * mm});
            skLineSegment(sketch, "E133.MirrorCS", {"start": v(14.79, -15.5) * mm, "end": v(14.79, -15) * mm});
            skArc(sketch, "E134.MirrorCS", {"start": v(14.79, -15.5) * mm, "mid": v(14.64, -15.85) * mm, "end": v(14.29, -16) * mm});
            skPoint(sketch, "E135.orphan", {"position": v(8.79, -14.5) * mm});
            skSolve(sketch);
        }
        {
            var Q0;
            Q0=qSketchRegion(id+"F5",true);
            extrude(context, id + "F6", {"entities" : qUnion([Q0]), "operationType" : NewBodyOperationType.ADD, "depth" : 3 * mm});
        }
        {
            var Q0;
            Q0=makeQuery(id+"F6.opExtrude","CAP_FACE",FACE,{"disambiguationData":[OSD([sQuery(id+"F5.wireOp",EDGE,"E105.bottom"),sQuery(id+"F5.wireOp",EDGE,"E105.top"),sQuery(id+"F5.wireOp",EDGE,"E105.left"),sQuery(id+"F5.wireOp",EDGE,"E105.right"),sQuery(id+"F5.wireOp",EDGE,"E106.left"),sQuery(id+"F5.wireOp",EDGE,"E106.right"),sQuery(id+"F5.wireOp",EDGE,"E107.bottom"),sQuery(id+"F5.wireOp",EDGE,"E107.top"),sQuery(id+"F5.wireOp",EDGE,"E107.left"),sQuery(id+"F5.wireOp",EDGE,"E107.right"),sQuery(id+"F5.wireOp",EDGE,"E108.filletArc"),sQuery(id+"F5.wireOp",EDGE,"E109.filletArc"),sQuery(id+"F5.wireOp",EDGE,"E110.filletArc"),sQuery(id+"F5.wireOp",EDGE,"E111.filletArc"),sQuery(id+"F5.wireOp",EDGE,"E113.filletArc"),sQuery(id+"F5.wireOp",EDGE,"E115.filletArc")])],"isStart":false});
            var sketch = newSketch(context, id + "F7", { "sketchPlane" : qUnion([Q0])});
            skPoint(sketch, "E136.firstSnap0", {"position": v(14.64, -4.65) * mm});
            skLineSegment(sketch, "E136.bottom", {"start": v(14.29, -4.5) * mm, "end": v(9.29, -4.5) * mm});
            skLineSegment(sketch, "E136.top", {"start": v(14.29, -7) * mm, "end": v(9.29, -7) * mm});
            skLineSegment(sketch, "E136.left", {"start": v(14.79, -5) * mm, "end": v(14.79, -6.5) * mm});
            skLineSegment(sketch, "E136.right", {"start": v(8.79, -5) * mm, "end": v(8.79, -6.5) * mm});
            skPoint(sketch, "E137.visualSharp", {"position": v(14.79, -4.5) * mm});
            skArc(sketch, "E137.filletArc", {"start": v(14.79, -5) * mm, "mid": v(14.64, -4.65) * mm, "end": v(14.29, -4.5) * mm});
            skPoint(sketch, "E138.visualSharp", {"position": v(8.79, -4.5) * mm});
            skArc(sketch, "E138.filletArc", {"start": v(9.29, -4.5) * mm, "mid": v(8.94, -4.65) * mm, "end": v(8.79, -5) * mm});
            skPoint(sketch, "E139.visualSharp", {"position": v(14.79, -7) * mm});
            skArc(sketch, "E139.filletArc", {"start": v(14.29, -7) * mm, "mid": v(14.64, -6.85) * mm, "end": v(14.79, -6.5) * mm});
            skLineSegment(sketch, "E140", {"start": v(8.79, -7) * mm, "end": v(8.79, -13.5) * mm, "construction": true});
            skPoint(sketch, "E141", {"position": v(8.79, -10.25) * mm});
            skLineSegment(sketch, "E142", {"start": v(8.79, -10.25) * mm, "end": v(15.78, -10.25) * mm, "construction": true});
            skLineSegment(sketch, "E143.MirrorCS", {"start": v(14.29, -13.5) * mm, "end": v(9.29, -13.5) * mm});
            skLineSegment(sketch, "E144.MirrorCS", {"start": v(8.79, -15.5) * mm, "end": v(8.79, -14) * mm});
            skLineSegment(sketch, "E145.MirrorCS", {"start": v(14.29, -16) * mm, "end": v(9.29, -16) * mm});
            skArc(sketch, "E146.MirrorCS", {"start": v(9.29, -16) * mm, "mid": v(8.94, -15.85) * mm, "end": v(8.79, -15.5) * mm});
            skArc(sketch, "E147.MirrorCS", {"start": v(14.79, -15.5) * mm, "mid": v(14.64, -15.85) * mm, "end": v(14.29, -16) * mm});
            skLineSegment(sketch, "E148.MirrorCS", {"start": v(14.79, -15.5) * mm, "end": v(14.79, -14) * mm});
            skArc(sketch, "E149.MirrorCS", {"start": v(14.29, -13.5) * mm, "mid": v(14.64, -13.65) * mm, "end": v(14.79, -14) * mm});
            skPoint(sketch, "E150.visualSharp", {"position": v(8.79, -7) * mm});
            skArc(sketch, "E150.filletArc", {"start": v(8.79, -6.5) * mm, "mid": v(8.94, -6.85) * mm, "end": v(9.29, -7) * mm});
            skPoint(sketch, "E151.visualSharp", {"position": v(8.79, -13.5) * mm});
            skArc(sketch, "E151.filletArc", {"start": v(9.29, -13.5) * mm, "mid": v(8.94, -13.65) * mm, "end": v(8.79, -14) * mm});
            skSolve(sketch);
        }
        {
            var Q0;
            Q0=makeQuery(id+"F7.imprint","IMPRINT",FACE,{"disambiguationData":[TD([[makeQuery(id+"F7.imprint","IMPRINT",EDGE,{"derivedFrom":sQuery(id+"F7.wireOp",EDGE,"E143.MirrorCS")}),1.0]])]});
            var Q1;
            Q1=makeQuery(id+"F7.imprint","IMPRINT",FACE,{"disambiguationData":[TD([[makeQuery(id+"F7.imprint","IMPRINT",EDGE,{"derivedFrom":sQuery(id+"F7.wireOp",EDGE,"E136.bottom")}),1.0]])]});
            var Q2;
            {var subQ0=sQuery(id+"F7.wireOp",EDGE,"E139.filletArc");Q2=makeQuery(id+"F7.imprint","IMPRINT",FACE,{"disambiguationData":[TD([[makeQuery(id+"F7.imprint","IMPRINT",EDGE,{"derivedFrom":subQ0}),1.0]])]});}
            extrude(context, id + "F8", {"entities" : qUnion([Q0, Q1, Q2]), "operationType" : NewBodyOperationType.ADD, "depth" : 2 * mm});
        }
        {
            var Q0;
            Q0=makeQuery(id+"F8.opExtrude","CAP_EDGE",EDGE,{"disambiguationData":[OSD([sQuery(id+"F7.wireOp",EDGE,"E145.MirrorCS")])],"isStart":false});
            var Q1;
            Q1=makeQuery(id+"F8.opExtrude","CAP_EDGE",EDGE,{"disambiguationData":[OSD([sQuery(id+"F7.wireOp",EDGE,"E143.MirrorCS")])],"isStart":false});
            var Q2;
            Q2=makeQuery(id+"F8.opExtrude","CAP_EDGE",EDGE,{"disambiguationData":[OSD([sQuery(id+"F7.wireOp",EDGE,"E151.filletArc")])],"isStart":false});
            var Q3;
            Q3=makeQuery(id+"F8.opExtrude","CAP_EDGE",EDGE,{"disambiguationData":[OSD([sQuery(id+"F7.wireOp",EDGE,"E144.MirrorCS")])],"isStart":false});
            var Q4;
            Q4=makeQuery(id+"F8.opExtrude","CAP_EDGE",EDGE,{"disambiguationData":[OSD([sQuery(id+"F7.wireOp",EDGE,"E146.MirrorCS")])],"isStart":false});
            var Q5;
            Q5=makeQuery(id+"F8.opExtrude","CAP_EDGE",EDGE,{"disambiguationData":[OSD([sQuery(id+"F7.wireOp",EDGE,"E147.MirrorCS")])],"isStart":false});
            var Q6;
            Q6=makeQuery(id+"F8.opExtrude","CAP_EDGE",EDGE,{"disambiguationData":[OSD([sQuery(id+"F7.wireOp",EDGE,"E148.MirrorCS")])],"isStart":false});
            var Q7;
            Q7=makeQuery(id+"F8.opExtrude","CAP_EDGE",EDGE,{"disambiguationData":[OSD([sQuery(id+"F7.wireOp",EDGE,"E149.MirrorCS")])],"isStart":false});
            var Q8;
            Q8=makeQuery(id+"F8.opExtrude","CAP_EDGE",EDGE,{"disambiguationData":[OSD([sQuery(id+"F7.wireOp",EDGE,"E136.top")])],"isStart":false});
            var Q9;
            Q9=makeQuery(id+"F8.opExtrude","CAP_EDGE",EDGE,{"disambiguationData":[OSD([sQuery(id+"F7.wireOp",EDGE,"E139.filletArc")])],"isStart":false});
            var Q10;
            Q10=makeQuery(id+"F8.opExtrude","CAP_EDGE",EDGE,{"disambiguationData":[OSD([sQuery(id+"F7.wireOp",EDGE,"E136.left")])],"isStart":false});
            var Q11;
            Q11=makeQuery(id+"F8.opExtrude","CAP_EDGE",EDGE,{"disambiguationData":[OSD([sQuery(id+"F7.wireOp",EDGE,"E136.bottom")])],"isStart":false});
            var Q12;
            Q12=makeQuery(id+"F8.opExtrude","CAP_EDGE",EDGE,{"disambiguationData":[OSD([sQuery(id+"F7.wireOp",EDGE,"E137.filletArc")])],"isStart":false});
            var Q13;
            Q13=makeQuery(id+"F8.opExtrude","CAP_EDGE",EDGE,{"disambiguationData":[OSD([sQuery(id+"F7.wireOp",EDGE,"E138.filletArc")])],"isStart":false});
            var Q14;
            Q14=makeQuery(id+"F8.opExtrude","CAP_EDGE",EDGE,{"disambiguationData":[OSD([sQuery(id+"F7.wireOp",EDGE,"E136.right")])],"isStart":false});
            var Q15;
            Q15=makeQuery(id+"F8.opExtrude","CAP_EDGE",EDGE,{"disambiguationData":[OSD([sQuery(id+"F7.wireOp",EDGE,"E150.filletArc")])],"isStart":false});
            fillet(context, id + "F9", {"entities" : qUnion([Q0, Q1, Q2, Q3, Q4, Q5, Q6, Q7, Q8, Q9, Q10, Q11, Q12, Q13, Q14, Q15]), "radius" : 1 * mm, "tangentPropagation" : true, "allowEdgeOverflow" : false});
        }
        {
            var Q0;
            Q0=makeQuery(id+"F6.opExtrude","CAP_EDGE",EDGE,{"disambiguationData":[OSD([sQuery(id+"F5.wireOp",EDGE,"E122.MirrorCS")])],"isStart":false});
            var Q1;
            Q1=makeQuery(id+"F6.opExtrude","CAP_EDGE",EDGE,{"disambiguationData":[OSD([sQuery(id+"F5.wireOp",EDGE,"E109.filletArc")])],"isStart":false});
            fillet(context, id + "F10", {"entities" : qUnion([Q0, Q1]), "radius" : .5 * mm, "tangentPropagation" : true, "allowEdgeOverflow" : false});
        }
        {
            var Q0;
            Q0=makeQuery(id+"F1.opExtrude","CAP_EDGE",EDGE,{"disambiguationData":[OSD([sQuery(id+"F0.wireOp",EDGE,"E42.left")])],"isStart":false});
            var Q1;
            Q1=makeQuery(id+"F1.opExtrude","CAP_EDGE",EDGE,{"disambiguationData":[OSD([sQuery(id+"F0.wireOp",EDGE,"E20")])],"isStart":false});
            var Q2;
            Q2=makeQuery(id+"F1.opExtrude","CAP_EDGE",EDGE,{"disambiguationData":[OSD([sQuery(id+"F0.wireOp",EDGE,"E12.MirrorCS")])],"isStart":false});
            var Q3;
            Q3=makeQuery(id+"F1.opExtrude","CAP_EDGE",EDGE,{"disambiguationData":[OSD([sQuery(id+"F0.wireOp",EDGE,"E13")])],"isStart":false});
            var Q4;
            Q4=makeQuery(id+"F1.opExtrude","CAP_EDGE",EDGE,{"disambiguationData":[OSD([sQuery(id+"F0.wireOp",EDGE,"E14")])],"isStart":false});
            var Q5;
            Q5=makeQuery(id+"F1.opExtrude","CAP_EDGE",EDGE,{"disambiguationData":[OSD([sQuery(id+"F0.wireOp",EDGE,"E11.MirrorCS")])],"isStart":false});
            var Q6;
            Q6=makeQuery(id+"F1.opExtrude","CAP_EDGE",EDGE,{"disambiguationData":[OSD([sQuery(id+"F0.wireOp",EDGE,"E15.MirrorCS")])],"isStart":false});
            var Q7;
            Q7=makeQuery(id+"F1.opExtrude","CAP_EDGE",EDGE,{"disambiguationData":[OSD([sQuery(id+"F0.wireOp",EDGE,"E16.MirrorCS")])],"isStart":false});
            var Q8;
            Q8=makeQuery(id+"F1.opExtrude","CAP_EDGE",EDGE,{"disambiguationData":[OSD([sQuery(id+"F0.wireOp",EDGE,"E17.MirrorCS")])],"isStart":false});
            var Q9;
            Q9=makeQuery(id+"F1.opExtrude","CAP_EDGE",EDGE,{"disambiguationData":[OSD([sQuery(id+"F0.wireOp",EDGE,"E18.MirrorCS")])],"isStart":false});
            var Q10;
            Q10=makeQuery(id+"F1.opExtrude","CAP_EDGE",EDGE,{"disambiguationData":[OSD([sQuery(id+"F0.wireOp",EDGE,"E30.MirrorCS")])],"isStart":false});
            var Q11;
            Q11=makeQuery(id+"F1.opExtrude","CAP_EDGE",EDGE,{"disambiguationData":[OSD([sQuery(id+"F0.wireOp",EDGE,"E29.MirrorCS")])],"isStart":false});
            var Q12;
            Q12=makeQuery(id+"F1.opExtrude","CAP_EDGE",EDGE,{"disambiguationData":[OSD([sQuery(id+"F0.wireOp",EDGE,"E28.MirrorCS")])],"isStart":false});
            var Q13;
            Q13=makeQuery(id+"F1.opExtrude","CAP_EDGE",EDGE,{"disambiguationData":[OSD([sQuery(id+"F0.wireOp",EDGE,"E27.MirrorCS")])],"isStart":false});
            var Q14;
            Q14=makeQuery(id+"F1.opExtrude","CAP_EDGE",EDGE,{"disambiguationData":[OSD([sQuery(id+"F0.wireOp",EDGE,"E25.MirrorCS")])],"isStart":false});
            var Q15;
            Q15=makeQuery(id+"F1.opExtrude","CAP_EDGE",EDGE,{"disambiguationData":[OSD([sQuery(id+"F0.wireOp",EDGE,"E21.MirrorCS")])],"isStart":false});
            var Q16;
            Q16=makeQuery(id+"F1.opExtrude","CAP_EDGE",EDGE,{"disambiguationData":[OSD([sQuery(id+"F0.wireOp",EDGE,"E24.MirrorCS")])],"isStart":false});
            var Q17;
            Q17=makeQuery(id+"F1.opExtrude","CAP_EDGE",EDGE,{"disambiguationData":[OSD([sQuery(id+"F0.wireOp",EDGE,"E23.MirrorCS")])],"isStart":false});
            var Q18;
            Q18=makeQuery(id+"F1.opExtrude","CAP_EDGE",EDGE,{"disambiguationData":[OSD([sQuery(id+"F0.wireOp",EDGE,"E22.MirrorCS")])],"isStart":false});
            var Q19;
            Q19=makeQuery(id+"F1.opExtrude","CAP_EDGE",EDGE,{"disambiguationData":[OSD([sQuery(id+"F0.wireOp",EDGE,"E26.MirrorCS")])],"isStart":false});
            var Q20;
            Q20=makeQuery(id+"F1.opExtrude","CAP_EDGE",EDGE,{"disambiguationData":[OSD([sQuery(id+"F0.wireOp",EDGE,"E42.right")])],"isStart":true});
            var Q21;
            Q21=makeQuery(id+"F1.opExtrude","CAP_EDGE",EDGE,{"disambiguationData":[OSD([sQuery(id+"F0.wireOp",EDGE,"E25.MirrorCS")])],"isStart":true});
            var Q22;
            Q22=makeQuery(id+"F1.opExtrude","CAP_EDGE",EDGE,{"disambiguationData":[OSD([sQuery(id+"F0.wireOp",EDGE,"E24.MirrorCS")])],"isStart":true});
            var Q23;
            Q23=makeQuery(id+"F1.opExtrude","CAP_EDGE",EDGE,{"disambiguationData":[OSD([sQuery(id+"F0.wireOp",EDGE,"E21.MirrorCS")])],"isStart":true});
            var Q24;
            Q24=makeQuery(id+"F1.opExtrude","CAP_EDGE",EDGE,{"disambiguationData":[OSD([sQuery(id+"F0.wireOp",EDGE,"E23.MirrorCS")])],"isStart":true});
            var Q25;
            Q25=makeQuery(id+"F1.opExtrude","CAP_EDGE",EDGE,{"disambiguationData":[OSD([sQuery(id+"F0.wireOp",EDGE,"E26.MirrorCS")])],"isStart":true});
            var Q26;
            Q26=makeQuery(id+"F1.opExtrude","CAP_EDGE",EDGE,{"disambiguationData":[OSD([sQuery(id+"F0.wireOp",EDGE,"E30.MirrorCS")])],"isStart":true});
            var Q27;
            Q27=makeQuery(id+"F1.opExtrude","CAP_EDGE",EDGE,{"disambiguationData":[OSD([sQuery(id+"F0.wireOp",EDGE,"E29.MirrorCS")])],"isStart":true});
            var Q28;
            Q28=makeQuery(id+"F1.opExtrude","CAP_EDGE",EDGE,{"disambiguationData":[OSD([sQuery(id+"F0.wireOp",EDGE,"E28.MirrorCS")])],"isStart":true});
            var Q29;
            Q29=makeQuery(id+"F1.opExtrude","CAP_EDGE",EDGE,{"disambiguationData":[OSD([sQuery(id+"F0.wireOp",EDGE,"E27.MirrorCS")])],"isStart":true});
            var Q30;
            Q30=makeQuery(id+"F1.opExtrude","CAP_EDGE",EDGE,{"disambiguationData":[OSD([sQuery(id+"F0.wireOp",EDGE,"E17.MirrorCS")])],"isStart":true});
            var Q31;
            Q31=makeQuery(id+"F1.opExtrude","CAP_EDGE",EDGE,{"disambiguationData":[OSD([sQuery(id+"F0.wireOp",EDGE,"E18.MirrorCS")])],"isStart":true});
            var Q32;
            Q32=makeQuery(id+"F1.opExtrude","CAP_EDGE",EDGE,{"disambiguationData":[OSD([sQuery(id+"F0.wireOp",EDGE,"E20")])],"isStart":true});
            var Q33;
            Q33=makeQuery(id+"F1.opExtrude","CAP_EDGE",EDGE,{"disambiguationData":[OSD([sQuery(id+"F0.wireOp",EDGE,"E11.MirrorCS")])],"isStart":true});
            var Q34;
            Q34=makeQuery(id+"F1.opExtrude","CAP_EDGE",EDGE,{"disambiguationData":[OSD([sQuery(id+"F0.wireOp",EDGE,"E14")])],"isStart":true});
            var Q35;
            Q35=makeQuery(id+"F1.opExtrude","CAP_EDGE",EDGE,{"disambiguationData":[OSD([sQuery(id+"F0.wireOp",EDGE,"E13")])],"isStart":true});
            var Q36;
            Q36=makeQuery(id+"F1.opExtrude","CAP_EDGE",EDGE,{"disambiguationData":[OSD([sQuery(id+"F0.wireOp",EDGE,"E16.MirrorCS")])],"isStart":true});
            var Q37;
            Q37=makeQuery(id+"F1.opExtrude","CAP_EDGE",EDGE,{"disambiguationData":[OSD([sQuery(id+"F0.wireOp",EDGE,"E15.MirrorCS")])],"isStart":true});
            var Q38;
            Q38=makeQuery(id+"F1.opExtrude","CAP_EDGE",EDGE,{"disambiguationData":[OSD([sQuery(id+"F0.wireOp",EDGE,"E19")])],"isStart":true});
            var Q39;
            Q39=makeQuery(id+"F1.opExtrude","CAP_EDGE",EDGE,{"disambiguationData":[OSD([sQuery(id+"F0.wireOp",EDGE,"E12.MirrorCS")])],"isStart":true});
            fillet(context, id + "F11", {"entities" : qUnion([Q0, Q1, Q2, Q3, Q4, Q5, Q6, Q7, Q8, Q9, Q10, Q11, Q12, Q13, Q14, Q15, Q16, Q17, Q18, Q19, Q20, Q21, Q22, Q23, Q24, Q25, Q26, Q27, Q28, Q29, Q30, Q31, Q32, Q33, Q34, Q35, Q36, Q37, Q38, Q39]), "radius" : .5 * mm, "tangentPropagation" : true, "allowEdgeOverflow" : false});
        }
        {
            var Q0;
            Q0=makeQuery(id+"F1.opExtrude","CAP_EDGE",EDGE,{"disambiguationData":[OSD([sQuery(id+"F0.wireOp",EDGE,"E49.MirrorCS")])],"isStart":true});
            var Q1;
            Q1=makeQuery(id+"F1.opExtrude","CAP_EDGE",EDGE,{"disambiguationData":[OSD([sQuery(id+"F0.wireOp",EDGE,"E63.MirrorCS")])],"isStart":true});
            var Q2;
            Q2=makeQuery(id+"F1.opExtrude","CAP_EDGE",EDGE,{"disambiguationData":[OSD([sQuery(id+"F0.wireOp",EDGE,"E49.MirrorCS")])],"isStart":false});
            var Q3;
            Q3=makeQuery(id+"F1.opExtrude","CAP_EDGE",EDGE,{"disambiguationData":[OSD([sQuery(id+"F0.wireOp",EDGE,"E63.MirrorCS")])],"isStart":false});
            fillet(context, id + "F12", {"entities" : qUnion([Q0, Q1, Q2, Q3]), "radius" : .5 * mm, "tangentPropagation" : true, "allowEdgeOverflow" : false});
        }
        {
            var Q0;
            Q0=makeQuery(id+"F1.opExtrude","CAP_EDGE",EDGE,{"disambiguationData":[OSD([sQuery(id+"F0.wireOp",EDGE,"E48")])],"isStart":false});
            var Q1;
            Q1=makeQuery(id+"F1.opExtrude","CAP_EDGE",EDGE,{"disambiguationData":[OSD([sQuery(id+"F0.wireOp",EDGE,"E31")])],"isStart":false});
            var Q2;
            Q2=makeQuery(id+"F1.opExtrude","CAP_EDGE",EDGE,{"disambiguationData":[OSD([sQuery(id+"F0.wireOp",EDGE,"E33.MirrorCS")])],"isStart":false});
            var Q3;
            Q3=makeQuery(id+"F1.opExtrude","CAP_EDGE",EDGE,{"disambiguationData":[OSD([sQuery(id+"F0.wireOp",EDGE,"E70.MirrorCS")])],"isStart":false});
            var Q4;
            Q4=makeQuery(id+"F1.opExtrude","CAP_EDGE",EDGE,{"disambiguationData":[OSD([sQuery(id+"F0.wireOp",EDGE,"E65.MirrorCS")])],"isStart":false});
            var Q5;
            Q5=makeQuery(id+"F1.opExtrude","CAP_EDGE",EDGE,{"disambiguationData":[OSD([sQuery(id+"F0.wireOp",EDGE,"E47")])],"isStart":false});
            var Q6;
            Q6=makeQuery(id+"F1.opExtrude","CAP_EDGE",EDGE,{"disambiguationData":[OSD([sQuery(id+"F0.wireOp",EDGE,"29c33aa2-e30d-4d77-a239-c7a4e06ad0fa.trimOffspring")])],"isStart":false});
            var Q7;
            Q7=makeQuery(id+"F1.opExtrude","CAP_EDGE",EDGE,{"disambiguationData":[OSD([sQuery(id+"F0.wireOp",EDGE,"E79.trimOffspring")])],"isStart":false});
            var Q8;
            Q8=makeQuery(id+"F1.opExtrude","CAP_EDGE",EDGE,{"disambiguationData":[OSD([sQuery(id+"F0.wireOp",EDGE,"E34.MirrorCS")])],"isStart":false});
            var Q9;
            Q9=makeQuery(id+"F1.opExtrude","CAP_EDGE",EDGE,{"disambiguationData":[OSD([sQuery(id+"F0.wireOp",EDGE,"E78.trimOffspring")])],"isStart":false});
            var Q10;
            Q10=makeQuery(id+"F1.opExtrude","CAP_EDGE",EDGE,{"disambiguationData":[OSD([sQuery(id+"F0.wireOp",EDGE,"E40.trimOffspring")])],"isStart":false});
            var Q11;
            Q11=makeQuery(id+"F1.opExtrude","CAP_EDGE",EDGE,{"disambiguationData":[OSD([sQuery(id+"F0.wireOp",EDGE,"E5")])],"isStart":false});
            var Q12;
            Q12=makeQuery(id+"F1.opExtrude","CAP_EDGE",EDGE,{"disambiguationData":[OSD([sQuery(id+"F0.wireOp",EDGE,"E33.MirrorCS")])],"isStart":true});
            var Q13;
            Q13=makeQuery(id+"F1.opExtrude","CAP_EDGE",EDGE,{"disambiguationData":[OSD([sQuery(id+"F0.wireOp",EDGE,"E2.MirrorC")])],"isStart":true});
            var Q14;
            Q14=makeQuery(id+"F1.opExtrude","CAP_EDGE",EDGE,{"disambiguationData":[OSD([sQuery(id+"F0.wireOp",EDGE,"E78.trimOffspring")])],"isStart":true});
            var Q15;
            Q15=makeQuery(id+"F1.opExtrude","CAP_EDGE",EDGE,{"disambiguationData":[OSD([sQuery(id+"F0.wireOp",EDGE,"E40.trimOffspring")])],"isStart":true});
            var Q16;
            Q16=makeQuery(id+"F1.opExtrude","CAP_EDGE",EDGE,{"disambiguationData":[OSD([sQuery(id+"F0.wireOp",EDGE,"E5")])],"isStart":true});
            var Q17;
            Q17=makeQuery(id+"F1.opExtrude","CAP_EDGE",EDGE,{"disambiguationData":[OSD([sQuery(id+"F0.wireOp",EDGE,"E1")])],"isStart":true});
            var Q18;
            Q18=makeQuery(id+"F1.opExtrude","CAP_EDGE",EDGE,{"disambiguationData":[OSD([sQuery(id+"F0.wireOp",EDGE,"E31")])],"isStart":true});
            var Q19;
            Q19=makeQuery(id+"F1.opExtrude","CAP_EDGE",EDGE,{"disambiguationData":[OSD([sQuery(id+"F0.wireOp",EDGE,"E48")])],"isStart":true});
            var Q20;
            Q20=makeQuery(id+"F1.opExtrude","CAP_EDGE",EDGE,{"disambiguationData":[OSD([sQuery(id+"F0.wireOp",EDGE,"E47")])],"isStart":true});
            var Q21;
            Q21=makeQuery(id+"F1.opExtrude","CAP_EDGE",EDGE,{"disambiguationData":[OSD([sQuery(id+"F0.wireOp",EDGE,"E70.MirrorCS")])],"isStart":true});
            var Q22;
            Q22=makeQuery(id+"F1.opExtrude","CAP_EDGE",EDGE,{"disambiguationData":[OSD([sQuery(id+"F0.wireOp",EDGE,"E65.MirrorCS")])],"isStart":true});
            var Q23;
            Q23=makeQuery(id+"F1.opExtrude","CAP_EDGE",EDGE,{"disambiguationData":[OSD([sQuery(id+"F0.wireOp",EDGE,"E34.MirrorCS")])],"isStart":true});
            var Q24;
            Q24=makeQuery(id+"F1.opExtrude","CAP_EDGE",EDGE,{"disambiguationData":[OSD([sQuery(id+"F0.wireOp",EDGE,"E35.MirrorCS")])],"isStart":true});
            var Q25;
            Q25=makeQuery(id+"F1.opExtrude","CAP_EDGE",EDGE,{"disambiguationData":[OSD([sQuery(id+"F0.wireOp",EDGE,"E4.MirrorC")])],"isStart":true});
            var Q26;
            Q26=makeQuery(id+"F1.opExtrude","CAP_EDGE",EDGE,{"disambiguationData":[OSD([sQuery(id+"F0.wireOp",EDGE,"E3.MirrorC")])],"isStart":true});
            var Q27;
            Q27=makeQuery(id+"F1.opExtrude","CAP_EDGE",EDGE,{"disambiguationData":[OSD([sQuery(id+"F0.wireOp",EDGE,"29c33aa2-e30d-4d77-a239-c7a4e06ad0fa.trimOffspring")])],"isStart":true});
            var Q28;
            Q28=makeQuery(id+"F1.opExtrude","CAP_EDGE",EDGE,{"disambiguationData":[OSD([sQuery(id+"F0.wireOp",EDGE,"E32.MirrorCS")])],"isStart":true});
            var Q29;
            Q29=makeQuery(id+"F1.opExtrude","CAP_EDGE",EDGE,{"disambiguationData":[OSD([sQuery(id+"F0.wireOp",EDGE,"E79.trimOffspring")])],"isStart":true});
            var Q30;
            Q30=makeQuery(id+"F1.opExtrude","CAP_EDGE",EDGE,{"disambiguationData":[OSD([sQuery(id+"F0.wireOp",EDGE,"E32.MirrorCS")])],"isStart":false});
            var Q31;
            Q31=makeQuery(id+"F1.opExtrude","CAP_EDGE",EDGE,{"disambiguationData":[OSD([sQuery(id+"F0.wireOp",EDGE,"E35.MirrorCS")])],"isStart":false});
            fillet(context, id + "F13", {"entities" : qUnion([Q0, Q1, Q2, Q3, Q4, Q5, Q6, Q7, Q8, Q9, Q10, Q11, Q12, Q13, Q14, Q15, Q16, Q17, Q18, Q19, Q20, Q21, Q22, Q23, Q24, Q25, Q26, Q27, Q28, Q29, Q30, Q31]), "radius" : .5 * mm, "tangentPropagation" : true, "allowEdgeOverflow" : false});
        }
        {
            var Q0;
            Q0=makeQuery(id+"F2.opExtrude","CAP_FACE",FACE,{"disambiguationData":[OSD([sQuery(id+"F0.wireOp",EDGE,"E3.MirrorC"),sQuery(id+"F0.wireOp",EDGE,"E9.MirrorC")])],"isStart":false});
            var sketch = newSketch(context, id + "F14", { "sketchPlane" : qUnion([Q0])});
            skCircle(sketch, "E152", {"center": v(-38.25, -49) * mm, "radius": 5.75 * mm});
            skCircle(sketch, "E153", {"center": v(-38.25, -49) * mm, "radius": 2.5 * mm});
            skCircle(sketch, "E154.MirrorC", {"center": v(38.25, -49) * mm, "radius": 5.75 * mm});
            skCircle(sketch, "E155.MirrorC", {"center": v(38.25, -49) * mm, "radius": 2.5 * mm});
            skCircle(sketch, "E156.MirrorC", {"center": v(-38.25, 49) * mm, "radius": 5.75 * mm});
            skCircle(sketch, "E157.MirrorC", {"center": v(-38.25, 49) * mm, "radius": 2.5 * mm});
            skCircle(sketch, "E158.MirrorC", {"center": v(38.25, 49) * mm, "radius": 5.75 * mm});
            skCircle(sketch, "E159.MirrorC", {"center": v(38.25, 49) * mm, "radius": 2.5 * mm});
            skSolve(sketch);
        }
        {
            var Q0;
            Q0=qSketchRegion(id+"F14",true);
            extrude(context, id + "F15", {"entities" : qUnion([Q0]), "operationType" : NewBodyOperationType.ADD, "depth" : .5 * mm});
        }
        {
            var Q0;
            Q0=makeQuery(id+"F2.opExtrude","CAP_EDGE",EDGE,{"disambiguationData":[OSD([sQuery(id+"F0.wireOp",EDGE,"E9.MirrorC")])],"isStart":true});
            var Q1;
            Q1=makeQuery(id+"F15.opExtrude","CAP_EDGE",EDGE,{"disambiguationData":[OSD([sQuery(id+"F14.wireOp",EDGE,"E153")])],"isStart":false});
            var Q2;
            Q2=makeQuery(id+"F15.opExtrude","CAP_EDGE",EDGE,{"disambiguationData":[OSD([sQuery(id+"F14.wireOp",EDGE,"E152")])],"isStart":false});
            var Q3;
            Q3=makeQuery(id+"F2.opExtrude","CAP_EDGE",EDGE,{"disambiguationData":[OSD([sQuery(id+"F0.wireOp",EDGE,"E3.MirrorC")])],"isStart":true});
            var Q4;
            Q4=makeQuery(id+"F15.opExtrude","CAP_EDGE",EDGE,{"disambiguationData":[OSD([sQuery(id+"F14.wireOp",EDGE,"E154.MirrorC")])],"isStart":false});
            var Q5;
            Q5=makeQuery(id+"F15.opExtrude","CAP_EDGE",EDGE,{"disambiguationData":[OSD([sQuery(id+"F14.wireOp",EDGE,"E155.MirrorC")])],"isStart":false});
            var Q6;
            Q6=makeQuery(id+"F2.opExtrude","CAP_EDGE",EDGE,{"disambiguationData":[OSD([sQuery(id+"F0.wireOp",EDGE,"E4.MirrorC")])],"isStart":true});
            var Q7;
            Q7=makeQuery(id+"F2.opExtrude","CAP_EDGE",EDGE,{"disambiguationData":[OSD([sQuery(id+"F0.wireOp",EDGE,"E7.MirrorC")])],"isStart":true});
            var Q8;
            Q8=makeQuery(id+"F15.opExtrude","CAP_EDGE",EDGE,{"disambiguationData":[OSD([sQuery(id+"F14.wireOp",EDGE,"E159.MirrorC")])],"isStart":false});
            var Q9;
            Q9=makeQuery(id+"F15.opExtrude","CAP_EDGE",EDGE,{"disambiguationData":[OSD([sQuery(id+"F14.wireOp",EDGE,"E158.MirrorC")])],"isStart":false});
            var Q10;
            Q10=makeQuery(id+"F2.opExtrude","CAP_EDGE",EDGE,{"disambiguationData":[OSD([sQuery(id+"F0.wireOp",EDGE,"E2.MirrorC")])],"isStart":true});
            var Q11;
            Q11=makeQuery(id+"F2.opExtrude","CAP_EDGE",EDGE,{"disambiguationData":[OSD([sQuery(id+"F0.wireOp",EDGE,"E1")])],"isStart":true});
            var Q12;
            Q12=makeQuery(id+"F2.opExtrude","CAP_EDGE",EDGE,{"disambiguationData":[OSD([sQuery(id+"F0.wireOp",EDGE,"E6")])],"isStart":true});
            var Q13;
            Q13=makeQuery(id+"F15.opExtrude","CAP_EDGE",EDGE,{"disambiguationData":[OSD([sQuery(id+"F14.wireOp",EDGE,"E156.MirrorC")])],"isStart":false});
            var Q14;
            Q14=makeQuery(id+"F15.opExtrude","CAP_EDGE",EDGE,{"disambiguationData":[OSD([sQuery(id+"F14.wireOp",EDGE,"E157.MirrorC")])],"isStart":false});
            var Q15;
            Q15=makeQuery(id+"F2.opExtrude","CAP_EDGE",EDGE,{"disambiguationData":[OSD([sQuery(id+"F0.wireOp",EDGE,"E8.MirrorC")])],"isStart":true});
            fillet(context, id + "F16", {"entities" : qUnion([Q0, Q1, Q2, Q3, Q4, Q5, Q6, Q7, Q8, Q9, Q10, Q11, Q12, Q13, Q14, Q15]), "radius" : .5 * mm, "tangentPropagation" : true, "allowEdgeOverflow" : false});
        }
    });
